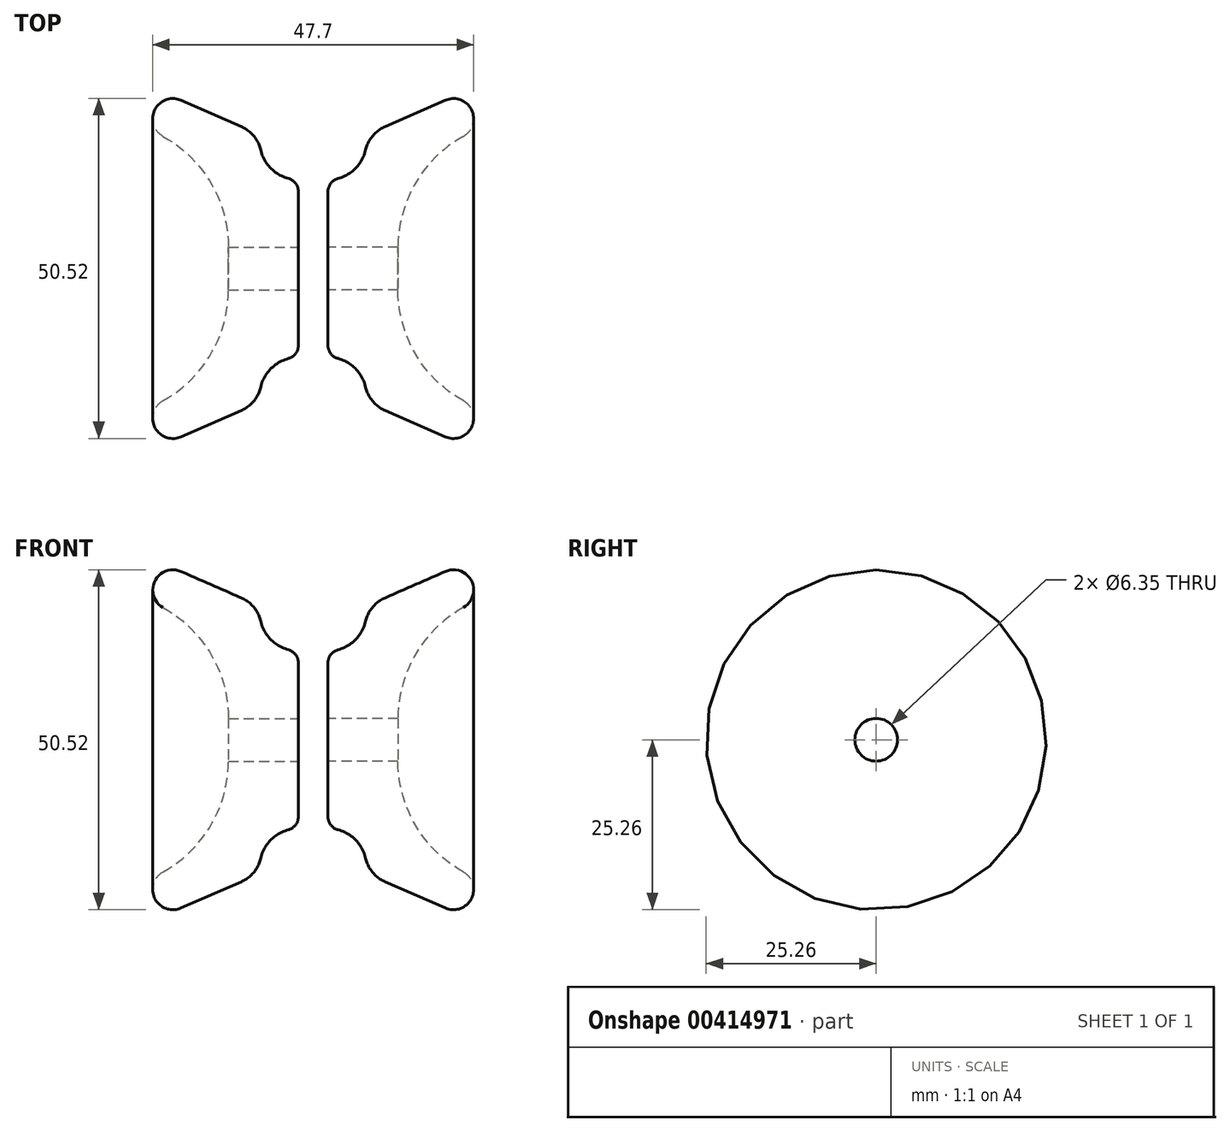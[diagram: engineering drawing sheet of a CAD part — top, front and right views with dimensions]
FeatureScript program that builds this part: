
annotation { "Feature Type Name" : "Feature", "Feature Type Description" : "" }
export const myFeature = defineFeature(function(context is Context, id is Id, definition is map)
    precondition{}
    {
        {
            var Q0;
            Q0=qCreatedBy(makeId("Front.planeOp"),FACE);
            var sketch = newSketch(context, id + "F0", { "sketchPlane" : qUnion([Q0])});
            skLineSegment(sketch, "E0", {"start": v(1.42, 0) * mm, "end": v(55.99, 0) * mm, "construction": true});
            skLineSegment(sketch, "E1", {"start": v(0, 0) * mm, "end": v(1.42, 0) * mm});
            skLineSegment(sketch, "E2", {"start": v(2.2, 3.18) * mm, "end": v(23.02, 3.18) * mm});
            skLineSegment(sketch, "E3", {"start": v(2.2, 3.18) * mm, "end": v(2.2, 11.44) * mm});
            skPoint(sketch, "E4.orphan", {"position": v(2.2, 28.4) * mm});
            skPoint(sketch, "E5.visualSharp", {"position": v(24.98, 28.4) * mm});
            skArc(sketch, "E5.filletArc", {"start": v(22.3, 19.63) * mm, "mid": v(23.53, 23.59) * mm, "end": v(19.64, 25) * mm});
            skPoint(sketch, "E6.visualSharp", {"position": v(5.24, 28.4) * mm});
            skLineSegment(sketch, "E7", {"start": v(19.64, 25) * mm, "end": v(10.67, 21.08) * mm});
            skArc(sketch, "E8", {"start": v(3.68, 13.37) * mm, "mid": v(6.33, 14.93) * mm, "end": v(7.8, 17.63) * mm});
            skLineSegment(sketch, "E9", {"start": v(2.2, 13.18) * mm, "end": v(10.07, 13.18) * mm, "construction": true});
            skArc(sketch, "E10", {"start": v(22.3, 19.63) * mm, "mid": v(15.21, 12.72) * mm, "end": v(12.61, 3.18) * mm});
            skPoint(sketch, "E11.visualSharp", {"position": v(7.87, 19.86) * mm});
            skArc(sketch, "E11.filletArc", {"start": v(10.67, 21.08) * mm, "mid": v(8.83, 19.7) * mm, "end": v(7.8, 17.63) * mm});
            skPoint(sketch, "E12.visualSharp", {"position": v(2.2, 13.18) * mm});
            skArc(sketch, "E12.filletArc", {"start": v(3.68, 13.37) * mm, "mid": v(2.61, 12.66) * mm, "end": v(2.2, 11.44) * mm});
            skSolve(sketch);
        }
        {
            var Q0;
            Q0 = qSketchRegion(id + "F0", true);
            var Q1;
            Q1=sQuery(id+"F0.wireOp",EDGE,"E0");
            revolve(context, id + "F1", {"entities" : qUnion([Q0]), "axis" : qUnion([Q1]), "revolveType" : RevolveType.FULL});
        }
        {
            var Q0;
            Q0=makeQuery(id+"F1.opRevolve","SWEPT_BODY",BODY,{"disambiguationData":[OSD([sQuery(id+"F0.wireOp",EDGE,"mZbOD1Ty-vybX-vjY0-FwbH-HTUoJSkJoMbB"),sQuery(id+"F0.wireOp",EDGE,"aBGLqhrI-tSyo-6gYt-KAye-IJAk45VHlq80"),sQuery(id+"F0.wireOp",EDGE,"E2"),sQuery(id+"F0.wireOp",EDGE,"E3"),sQuery(id+"F0.wireOp",EDGE,"nVWTpK0W-6udX-ogbc-4szu-DyMPWpEjQgmP")])]});
            var Q1;
            Q1=qCreatedBy(makeId("Right.planeOp"),FACE);
            mirror(context, id + "F2", {"operationType" : NewBodyOperationType.ADD, "entities" : qUnion([Q0]), "mirrorPlane" : qUnion([Q1])});
        }
    });
